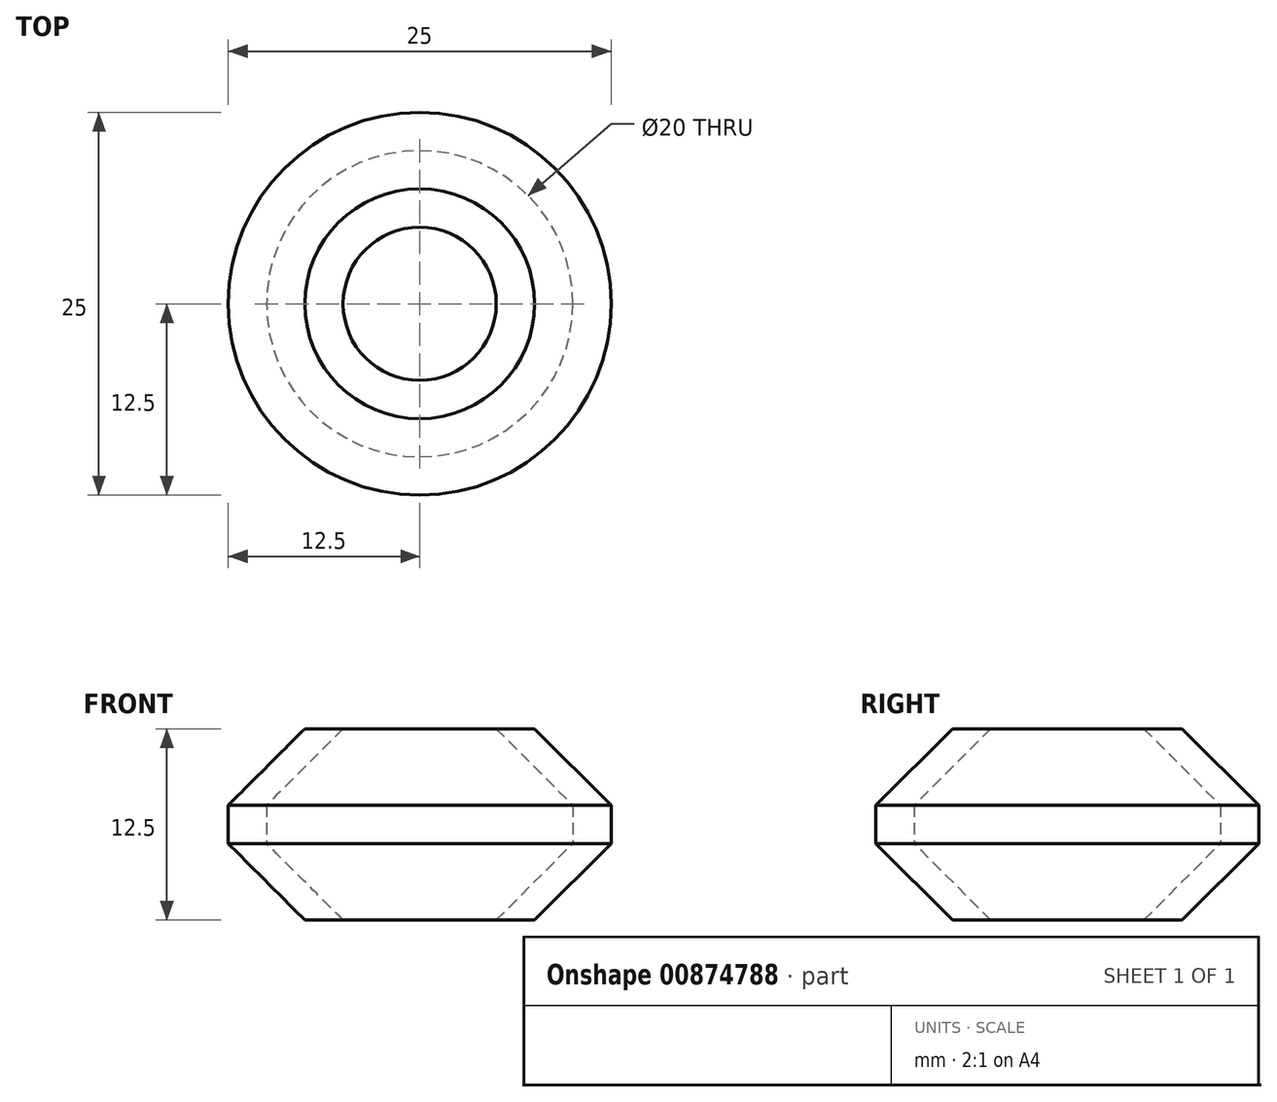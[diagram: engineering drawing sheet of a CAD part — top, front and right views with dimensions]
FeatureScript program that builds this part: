
annotation { "Feature Type Name" : "Feature", "Feature Type Description" : "" }
export const myFeature = defineFeature(function(context is Context, id is Id, definition is map)
    precondition{}
    {
        {
            var Q0;
            Q0=qCreatedBy(makeId("Front.planeOp"),FACE);
            var sketch = newSketch(context, id + "F0", { "sketchPlane" : qUnion([Q0])});
            skLineSegment(sketch, "E0", {"start": v(0, 0) * mm, "end": v(0, 5) * mm});
            skLineSegment(sketch, "E1", {"start": v(0, 5) * mm, "end": v(0, 7.5) * mm});
            skLineSegment(sketch, "E2", {"start": v(0, 7.5) * mm, "end": v(0, 12.5) * mm});
            skLineSegment(sketch, "E3", {"start": v(0, 7.5) * mm, "end": v(2.5, 7.5) * mm});
            skLineSegment(sketch, "E4", {"start": v(2.5, 7.5) * mm, "end": v(2.5, 5) * mm});
            skLineSegment(sketch, "E5", {"start": v(2.5, 5) * mm, "end": v(0, 5) * mm});
            skLineSegment(sketch, "E6", {"start": v(2.5, 7.5) * mm, "end": v(5, 7.5) * mm});
            skLineSegment(sketch, "E7", {"start": v(0, 7.5) * mm, "end": v(5, 12.5) * mm});
            skLineSegment(sketch, "E8", {"start": v(5, 12.5) * mm, "end": v(7.5, 12.5) * mm});
            skLineSegment(sketch, "E9", {"start": v(2.5, 7.5) * mm, "end": v(7.5, 12.5) * mm});
            skLineSegment(sketch, "E10", {"start": v(2.5, 5) * mm, "end": v(7.5, 0) * mm});
            skLineSegment(sketch, "E11", {"start": v(7.5, 0) * mm, "end": v(5, 0) * mm});
            skPoint(sketch, "E11.endSnap0", {"position": v(5, 2.5) * mm});
            skLineSegment(sketch, "E12", {"start": v(5, 0) * mm, "end": v(0, 5) * mm});
            skLineSegment(sketch, "E13", {"start": v(2.5, 6.25) * mm, "end": v(12.5, 6.25) * mm});
            skLineSegment(sketch, "E14", {"start": v(12.5, 6.25) * mm, "end": v(12.5, 12.4) * mm});
            skSolve(sketch);
        }
        {
            var Q0;
            Q0=makeQuery(id+"F0.imprint","IMPRINT",FACE,{"disambiguationData":[TD([[makeQuery(id+"F0.imprint","IMPRINT",EDGE,{"derivedFrom":sQuery(id+"F0.wireOp",EDGE,"E3")}),1.0]])]});
            var Q1;
            Q1=makeQuery(id+"F0.imprint","IMPRINT",FACE,{"disambiguationData":[TD([[makeQuery(id+"F0.imprint","IMPRINT",EDGE,{"derivedFrom":sQuery(id+"F0.wireOp",EDGE,"E1")}),-1.0]])]});
            var Q2;
            Q2=makeQuery(id+"F0.imprint","IMPRINT",FACE,{"disambiguationData":[TD([[makeQuery(id+"F0.imprint","IMPRINT",EDGE,{"derivedFrom":sQuery(id+"F0.wireOp",EDGE,"E5")}),1.0]])]});
            var Q3;
            Q3=sQuery(id+"F0.wireOp",EDGE,"E14");
            revolve(context, id + "F1", {"surfaceOperationType" : NewSurfaceOperationType.NEW, "entities" : qUnion([Q0, Q1, Q2]), "axis" : qUnion([Q3]), "revolveType" : RevolveType.FULL});
        }
    });
